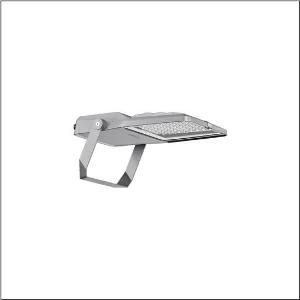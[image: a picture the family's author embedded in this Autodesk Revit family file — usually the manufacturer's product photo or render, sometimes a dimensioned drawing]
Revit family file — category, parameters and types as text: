
# Revit family: floodlight_fl_21_iq_mini___pl33t_5xa7772b4f1a_67af
name_source: partatom
category: Lighting Fixtures
units: mm (PartAtom-declared; Revit-internal decimal feet)

## family parameters
Cut with Voids When Loaded = No
Host = Face
Light Source = No
Part Type = Normal
Room Calculation Point = No
Round Connector Dimension = Use Diameter
Shared = No

## types (1)
- --- (1 x LED, 6420 lm, 45.5 W, 4000K)
    Apparent Load = 46 VA
    CIE Flux Codes = 26 75 99 100 100
    Color Rendering = 70
    Color Temperature = 4000K
    Default Elevation = 1800 mm
    Description = Floodlight FL 21 iQ mini, floodlight, primary light control with lens, of PMMA, primary optical cover: protective disc, of toughened safety glass, transparent, light distribution: PL33T, light emission: direct distribution, installation type: surface-mounted, LED, High Power LED, rated luminous flux: 6.420lm, luminous efficacy: 141lm/W, light colour: 740, colour temperature: 4000K, control: Street-Remote, Auto-Match, Temp-Guard, Night-Set, Smart-Wire, Desk-Remote (wireless, voltage-free reading and setting of iQ features in the workshop via application-optimized NFC function/RFID function), optimised constant luminous flux control (CLO 2.0), with terminal, 6-pole, mains connection: 220..240V, AC, 50/60Hz, start of lifetime: 46W, end of service life: 48W, reduction: 22W, luminaire housing, of diecast aluminium, powder-coated, Siteco® metallic grey (DB 702S), corrosivity category C5 mid according to DIN EN ISO 12944, sealing non-destructively replaceable, mounting bracket, of steel, galvanised, powder-coated, Siteco® metallic grey (DB 702S), protection rating (complete): IP66, insulation class (complete): insulation class II (safety insulation), certification: CE, ENEC, VDE, protection symbol: D, impact resistance: IK08, permissible operating ambient temperature: -40..+40°C, permissible operating ambient temperature for outdoor applications: -40..+50°C, standard: DIN EN 12944, LABS conformity tested according to VDMA 24364:2018-05, packaging unit: 1 piece

Light Distribution: PL33T
    Height = 70 mm
    Lamp = 1 x LED
    Lamp Light Flux = 6420 lm
    Lamp Power = 45.5 W
    Lamp count = 1
    Length = 485 mm
    Luminous efficacy = 141 lm/W
    Manufacturer = Siteco
    ModVariant = No
    Model = 5XA7772B4F1A
    Number of Poles = 1
    OnlyDefault = Yes
    Power Factor = 1
    Product Name = Floodlight FL 21 iQ mini | PL33T
    Product group = floodlight | pylon annexe
    ProductGroupID = 6200
    Protection Class = Protection class II
    Protection Degree = IP 66
    RLX_Detail_Level = 1
    RLX_Emergency_Light_Flux = 0 lm
    RLX_Emergency_Type = 0
    RLX_Emergency_Type_DB = No
    RlxData = <blob elided: 96061 chars, md5=49a196bc>
    Socket = socket
    Standby Power = 0 W
    System Light Flux = 6420 lm
    System Power = 46 W
    Type Comments = factory setting: luminous flux: 100 % | dim-lin: 254 | 463 mA
    Type Image = l_1006845.jpg
    URL = http://relux.com
    VarID = @adj_082443
    Voltage = 0 V
    Weight = 0.00 kg
    Width = 337 mm

## geometry (parser evidence)
native form markers: Blend x4, Sweep x10
no freeform markers — native parametric forms only
